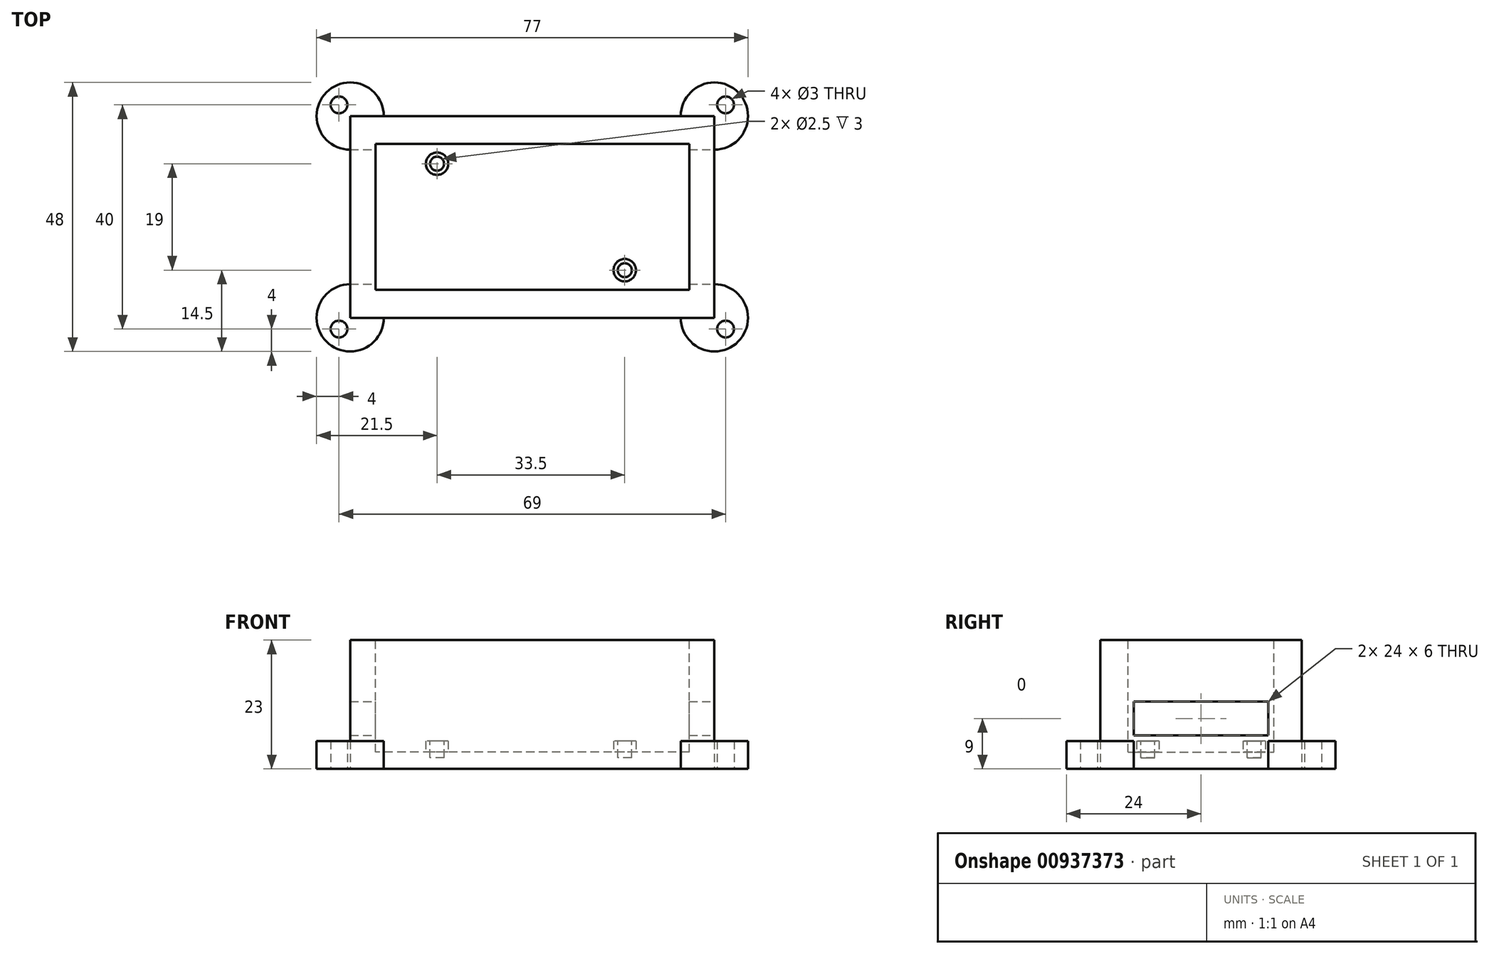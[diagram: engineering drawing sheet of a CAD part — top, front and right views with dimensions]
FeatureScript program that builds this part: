
annotation { "Feature Type Name" : "Feature", "Feature Type Description" : "" }
export const myFeature = defineFeature(function(context is Context, id is Id, definition is map)
    precondition{}
    {
        {
            var Q0;
            Q0=qCreatedBy(makeId("Top.planeOp"),FACE);
            var sketch = newSketch(context, id + "F0", { "sketchPlane" : qUnion([Q0])});
            skLineSegment(sketch, "E0.bottom", {"start": v(32.5, -18) * mm, "end": v(-32.5, -18) * mm});
            skLineSegment(sketch, "E0.top", {"start": v(32.5, 18) * mm, "end": v(-32.5, 18) * mm});
            skLineSegment(sketch, "E0.left", {"start": v(32.5, -18) * mm, "end": v(32.5, 18) * mm});
            skLineSegment(sketch, "E0.right", {"start": v(-32.5, -18) * mm, "end": v(-32.5, 18) * mm});
            skPoint(sketch, "E0.middle", {"position": v(0, 0) * mm});
            skSolve(sketch);
        }
        {
            var Q0;
            Q0 = qSketchRegion(id + "F0", true);
            extrude(context, id + "F1", {"entities" : qUnion([Q0]), "depth" : 23 * mm, "offsetDistance" : 25 * mm});
        }
        {
            var Q0;
            Q0=makeQuery(id+"F1.opExtrude","CAP_FACE",FACE,{"disambiguationData":[OSD([sQuery(id+"F0.wireOp",EDGE,"E0.bottom"),sQuery(id+"F0.wireOp",EDGE,"E0.top"),sQuery(id+"F0.wireOp",EDGE,"E0.left"),sQuery(id+"F0.wireOp",EDGE,"E0.right")])],"isStart":false});
            var sketch = newSketch(context, id + "F2", { "sketchPlane" : qUnion([Q0])});
            skLineSegment(sketch, "E1.bottom", {"start": v(28, -13) * mm, "end": v(-28, -13) * mm});
            skLineSegment(sketch, "E1.top", {"start": v(28, 13) * mm, "end": v(-28, 13) * mm});
            skLineSegment(sketch, "E1.left", {"start": v(28, -13) * mm, "end": v(28, 13) * mm});
            skLineSegment(sketch, "E1.right", {"start": v(-28, -13) * mm, "end": v(-28, 13) * mm});
            skPoint(sketch, "E1.middle", {"position": v(0, 0) * mm});
            skSolve(sketch);
        }
        {
            var Q0;
            Q0 = qSketchRegion(id + "F2", true);
            extrude(context, id + "F3", {"entities" : qUnion([Q0]), "operationType" : NewBodyOperationType.REMOVE, "oppositeDirection" : true, "depth" : 20 * mm, "offsetDistance" : 25 * mm});
        }
        {
            var Q0;
            Q0=makeQuery(id+"F3.boolean.opBoolean","COPY",FACE,{"derivedFrom":makeQuery(id+"F3.opExtrude","CAP_FACE",FACE,{"disambiguationData":[OSD([sQuery(id+"F2.wireOp",EDGE,"E1.bottom"),sQuery(id+"F2.wireOp",EDGE,"E1.top"),sQuery(id+"F2.wireOp",EDGE,"E1.left"),sQuery(id+"F2.wireOp",EDGE,"E1.right")])],"isStart":false})});
            var sketch = newSketch(context, id + "F4", { "sketchPlane" : qUnion([Q0])});
            skCircle(sketch, "E2", {"center": v(-17, 9.5) * mm, "radius": 2 * mm});
            skCircle(sketch, "E3", {"center": v(16.5, -9.5) * mm, "radius": 2 * mm});
            skSolve(sketch);
        }
        {
            var Q0;
            Q0 = qSketchRegion(id + "F4", true);
            extrude(context, id + "F5", {"entities" : qUnion([Q0]), "operationType" : NewBodyOperationType.ADD, "depth" : 2 * mm, "offsetDistance" : 25 * mm});
        }
        {
            var Q0;
            Q0=makeQuery(id+"F5.opExtrude","CAP_FACE",FACE,{"disambiguationData":[OSD([sQuery(id+"F4.wireOp",EDGE,"E2")])],"isStart":false});
            var sketch = newSketch(context, id + "F6", { "sketchPlane" : qUnion([Q0])});
            skCircle(sketch, "E4", {"center": v(-17, 9.5) * mm, "radius": 1.25 * mm});
            skSolve(sketch);
        }
        {
            var Q0;
            Q0 = qSketchRegion(id + "F6", true);
            extrude(context, id + "F7", {"entities" : qUnion([Q0]), "operationType" : NewBodyOperationType.REMOVE, "oppositeDirection" : true, "depth" : 3 * mm, "offsetDistance" : 25 * mm});
        }
        {
            var Q0;
            Q0=makeQuery(id+"F5.opExtrude","CAP_FACE",FACE,{"disambiguationData":[OSD([sQuery(id+"F4.wireOp",EDGE,"E3")])],"isStart":false});
            var sketch = newSketch(context, id + "F8", { "sketchPlane" : qUnion([Q0])});
            skCircle(sketch, "E5", {"center": v(16.5, -9.5) * mm, "radius": 1.25 * mm});
            skSolve(sketch);
        }
        {
            var Q0;
            Q0 = qSketchRegion(id + "F8", true);
            extrude(context, id + "F9", {"entities" : qUnion([Q0]), "operationType" : NewBodyOperationType.REMOVE, "oppositeDirection" : true, "depth" : 3 * mm, "offsetDistance" : 25 * mm});
        }
        {
            var Q0;
            Q0=makeQuery(id+"F1.opExtrude","CAP_FACE",FACE,{"disambiguationData":[OSD([sQuery(id+"F0.wireOp",EDGE,"E0.bottom"),sQuery(id+"F0.wireOp",EDGE,"E0.top"),sQuery(id+"F0.wireOp",EDGE,"E0.left"),sQuery(id+"F0.wireOp",EDGE,"E0.right")])],"isStart":true});
            var sketch = newSketch(context, id + "F10", { "sketchPlane" : qUnion([Q0])});
            skCircle(sketch, "E6", {"center": v(-32.5, 18) * mm, "radius": 6 * mm});
            skCircle(sketch, "E7", {"center": v(32.5, 18) * mm, "radius": 6 * mm});
            skCircle(sketch, "E8", {"center": v(32.5, -18) * mm, "radius": 6 * mm});
            skCircle(sketch, "E9", {"center": v(-32.5, -18) * mm, "radius": 6 * mm});
            skCircle(sketch, "E10", {"center": v(-34.5, 20) * mm, "radius": 1.5 * mm});
            skCircle(sketch, "E11", {"center": v(34.5, 20) * mm, "radius": 1.5 * mm});
            skCircle(sketch, "E12", {"center": v(34.5, -20) * mm, "radius": 1.5 * mm});
            skCircle(sketch, "E13", {"center": v(-34.5, -20) * mm, "radius": 1.5 * mm});
            skSolve(sketch);
        }
        {
            var Q0;
            Q0 = qSketchRegion(id + "F10", true);
            extrude(context, id + "F11", {"entities" : qUnion([Q0]), "operationType" : NewBodyOperationType.ADD, "oppositeDirection" : true, "depth" : 5 * mm, "offsetDistance" : 25 * mm});
        }
        {
            var Q0;
            Q0=makeQuery(id+"F1.opExtrude","SWEPT_FACE",FACE,{"disambiguationData":[OSD([sQuery(id+"F0.wireOp",EDGE,"E0.left")])]});
            var sketch = newSketch(context, id + "F12", { "sketchPlane" : qUnion([Q0])});
            skLineSegment(sketch, "E14.bottom", {"start": v(12, 6) * mm, "end": v(-12, 6) * mm});
            skLineSegment(sketch, "E14.top", {"start": v(12, 12) * mm, "end": v(-12, 12) * mm});
            skLineSegment(sketch, "E14.left", {"start": v(12, 6) * mm, "end": v(12, 12) * mm});
            skLineSegment(sketch, "E14.right", {"start": v(-12, 6) * mm, "end": v(-12, 12) * mm});
            skPoint(sketch, "E14.middle", {"position": v(0, 9) * mm});
            skSolve(sketch);
        }
        {
            var Q0;
            Q0 = qSketchRegion(id + "F12", true);
            extrude(context, id + "F13", {"entities" : qUnion([Q0]), "operationType" : NewBodyOperationType.REMOVE, "oppositeDirection" : true, "depth" : 100 * mm, "offsetDistance" : 25 * mm});
        }
    });
